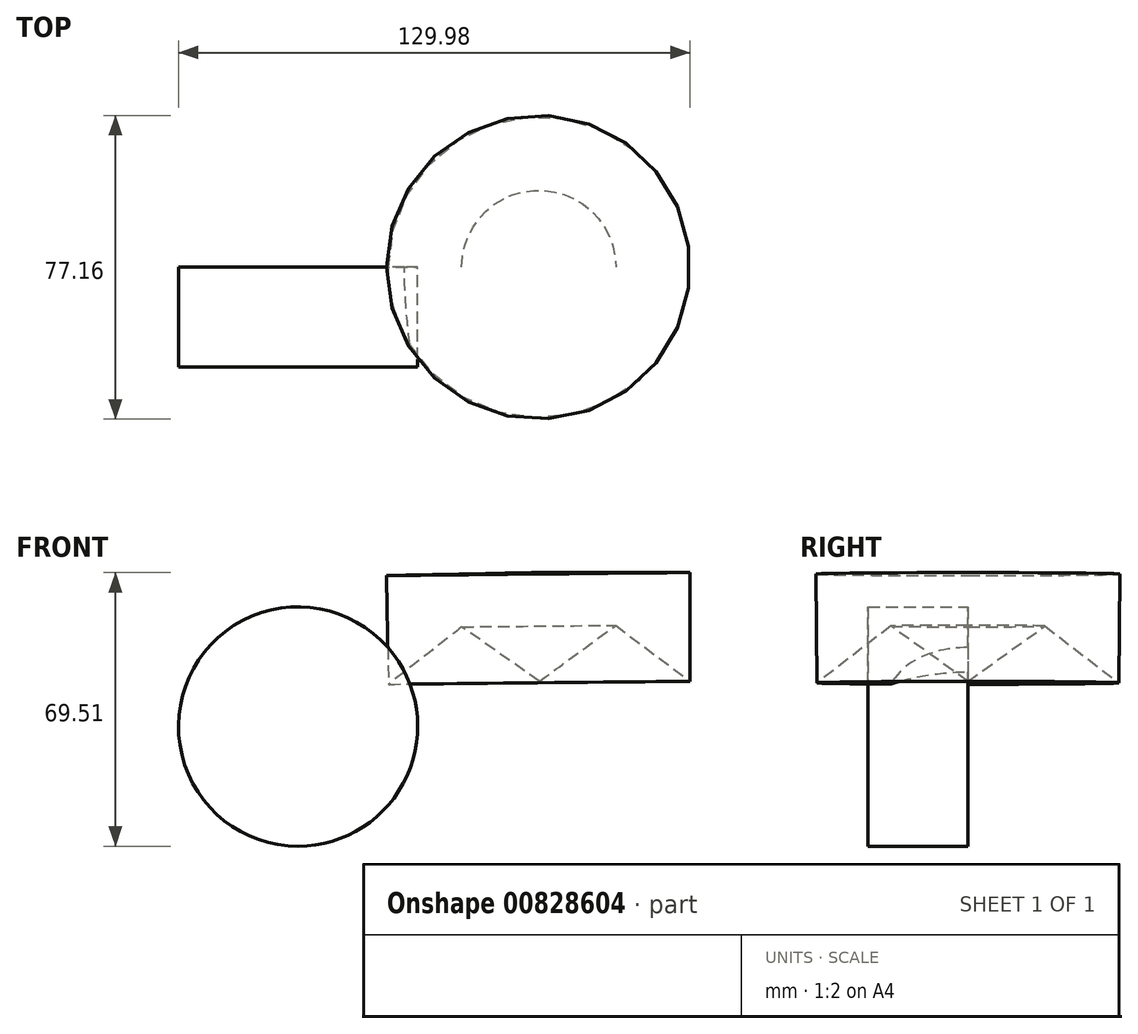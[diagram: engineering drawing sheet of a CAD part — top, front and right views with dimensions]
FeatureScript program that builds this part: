
annotation { "Feature Type Name" : "Feature", "Feature Type Description" : "" }
export const myFeature = defineFeature(function(context is Context, id is Id, definition is map)
    precondition{}
    {
        {
            var Q0;
            Q0=qCreatedBy(makeId("Front.planeOp"),FACE);
            var sketch = newSketch(context, id + "F0", { "sketchPlane" : qUnion([Q0])});
            skCircle(sketch, "E0", {"center": v(-41.45, 17.92) * mm, "radius": 30.39 * mm});
            skLineSegment(sketch, "E1", {"start": v(11.63, 47.47) * mm, "end": v(61.7, 52.94) * mm});
            skLineSegment(sketch, "E2", {"start": v(61.7, 52.94) * mm, "end": v(54.3, 23.67) * mm});
            skLineSegment(sketch, "E3", {"start": v(54.3, 23.67) * mm, "end": v(35.43, 34.06) * mm});
            skLineSegment(sketch, "E4", {"start": v(35.43, 34.06) * mm, "end": v(13.82, 19.01) * mm});
            skLineSegment(sketch, "E5", {"start": v(13.82, 19.01) * mm, "end": v(11.63, 47.47) * mm});
            skSolve(sketch);
        }
        {
            var Q0;
            Q0=makeQuery(id+"F0.imprint","IMPRINT",FACE,{"disambiguationData":[TD([[makeQuery(id+"F0.imprint","IMPRINT",EDGE,{"derivedFrom":sQuery(id+"F0.wireOp",EDGE,"E0")}),1.0]])]});
            extrude(context, id + "F1", {"entities" : qUnion([Q0]), "depth" : 25.4 * mm, "offsetDistance" : 25.4 * mm});
        }
        {
            var Q0;
            Q0=qCreatedBy(makeId("Front.planeOp"),FACE);
            var sketch = newSketch(context, id + "F2", { "sketchPlane" : qUnion([Q0])});
            skLineSegment(sketch, "E6", {"start": v(19.56, 57.04) * mm, "end": v(58.14, 57.04) * mm});
            skLineSegment(sketch, "E7", {"start": v(58.14, 57.04) * mm, "end": v(58.14, 29.41) * mm});
            skLineSegment(sketch, "E8", {"start": v(58.14, 29.41) * mm, "end": v(39.26, 43.64) * mm});
            skLineSegment(sketch, "E9", {"start": v(39.26, 43.64) * mm, "end": v(19.84, 29.41) * mm});
            skLineSegment(sketch, "E10", {"start": v(19.84, 29.41) * mm, "end": v(19.56, 57.04) * mm});
            skSolve(sketch);
        }
        {
            var Q0;
            Q0=makeQuery(id+"F2.imprint","IMPRINT",FACE,{"disambiguationData":[TD([[makeQuery(id+"F2.imprint","IMPRINT",EDGE,{"derivedFrom":sQuery(id+"F2.wireOp",EDGE,"E6")}),-1.0]])]});
            var Q1;
            Q1=sQuery(id+"F2.wireOp",EDGE,"E10");
            revolve(context, id + "F3", {"operationType" : NewBodyOperationType.ADD, "surfaceOperationType" : NewSurfaceOperationType.NEW, "entities" : qUnion([Q0]), "axis" : qUnion([Q1]), "revolveType" : RevolveType.FULL});
        }
    });
